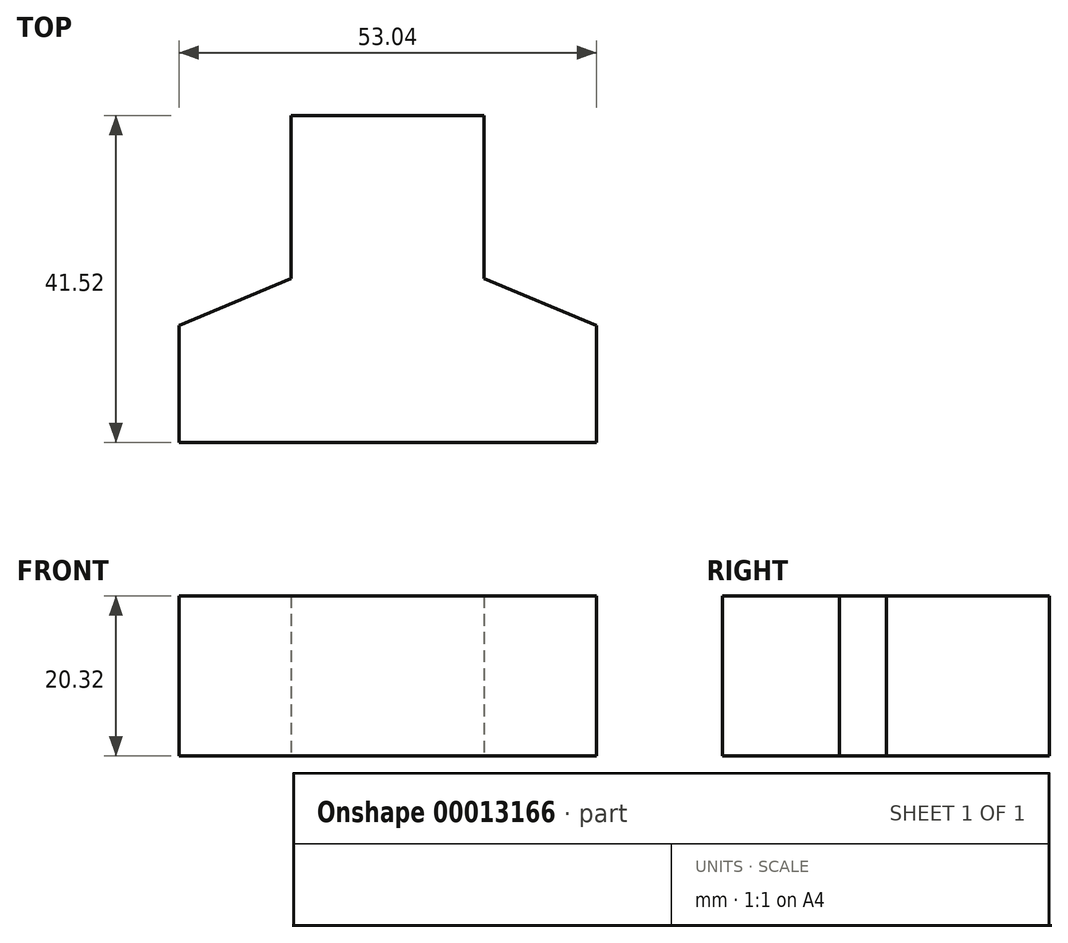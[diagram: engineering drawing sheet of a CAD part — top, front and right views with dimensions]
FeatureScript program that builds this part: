
annotation { "Feature Type Name" : "Feature", "Feature Type Description" : "" }
export const myFeature = defineFeature(function(context is Context, id is Id, definition is map)
    precondition{}
    {
        {
            var Q0;
            Q0=qCreatedBy(makeId("Top.planeOp"),FACE);
            var sketch = newSketch(context, id + "F0", { "sketchPlane" : qUnion([Q0])});
            skLineSegment(sketch, "E0", {"start": v(-10.06, 57.15) * mm, "end": v(14.46, 57.15) * mm});
            skLineSegment(sketch, "E1", {"start": v(14.46, 57.15) * mm, "end": v(14.46, 36.45) * mm});
            skLineSegment(sketch, "E2", {"start": v(14.46, 36.45) * mm, "end": v(28.72, 30.46) * mm});
            skLineSegment(sketch, "E3", {"start": v(28.72, 30.46) * mm, "end": v(28.72, 15.63) * mm});
            skLineSegment(sketch, "E4", {"start": v(28.72, 15.63) * mm, "end": v(-24.32, 15.63) * mm});
            skLineSegment(sketch, "E5", {"start": v(-24.32, 15.63) * mm, "end": v(-24.32, 30.46) * mm});
            skLineSegment(sketch, "E6", {"start": v(-24.32, 30.46) * mm, "end": v(-10.06, 36.45) * mm});
            skLineSegment(sketch, "E7", {"start": v(-10.06, 36.45) * mm, "end": v(-10.06, 57.15) * mm});
            skSolve(sketch);
        }
        {
            var Q0;
            Q0 = qSketchRegion(id + "F0", true);
            extrude(context, id + "F1", {"entities" : qUnion([Q0]), "depth" : 20.32 * mm});
        }
    });
